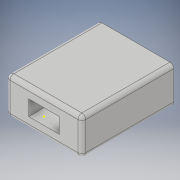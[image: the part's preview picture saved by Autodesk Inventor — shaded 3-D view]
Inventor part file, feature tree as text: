
AUTODESK INVENTOR PART (.ipt)
format: ipt  version: 2019 (Build 230136000, 136)  size: 140,800 bytes
history: native  units: mm
features: sketch x4, extrude x2, fillet x1, projected_geometry x1
ambient origin geometry x8: Origin, YZ Plane, XZ Plane, XY Plane, X Axis, Y Axis, Z Axis, Center Point
bodies: Solid1 (feature_tree)
feature tree (8):
  sketch  "Sketch1"  dims[d0=35.5mm d2=16.0mm]
  sketch  "Sketch2"  dims[d3=13.0mm d8=35.5mm d9=15.0mm]
  extrude  "Extrusion1"  Depth=16.0mm
  extrude  "Extrusion2"  Depth=35.5mm
  sketch  "Sketch4"  dims[d11=20.0mm d12=0.0mm d13=16.0mm d14=8.0mm d15=28.0mm d16=0.0mm d17=2.0mm]
  fillet  "Fillet1"  Radius=15.0mm
  sketch  "Sketch3"  dims[d10=2.0mm]
  projected_geometry  "Projected Loop1"
